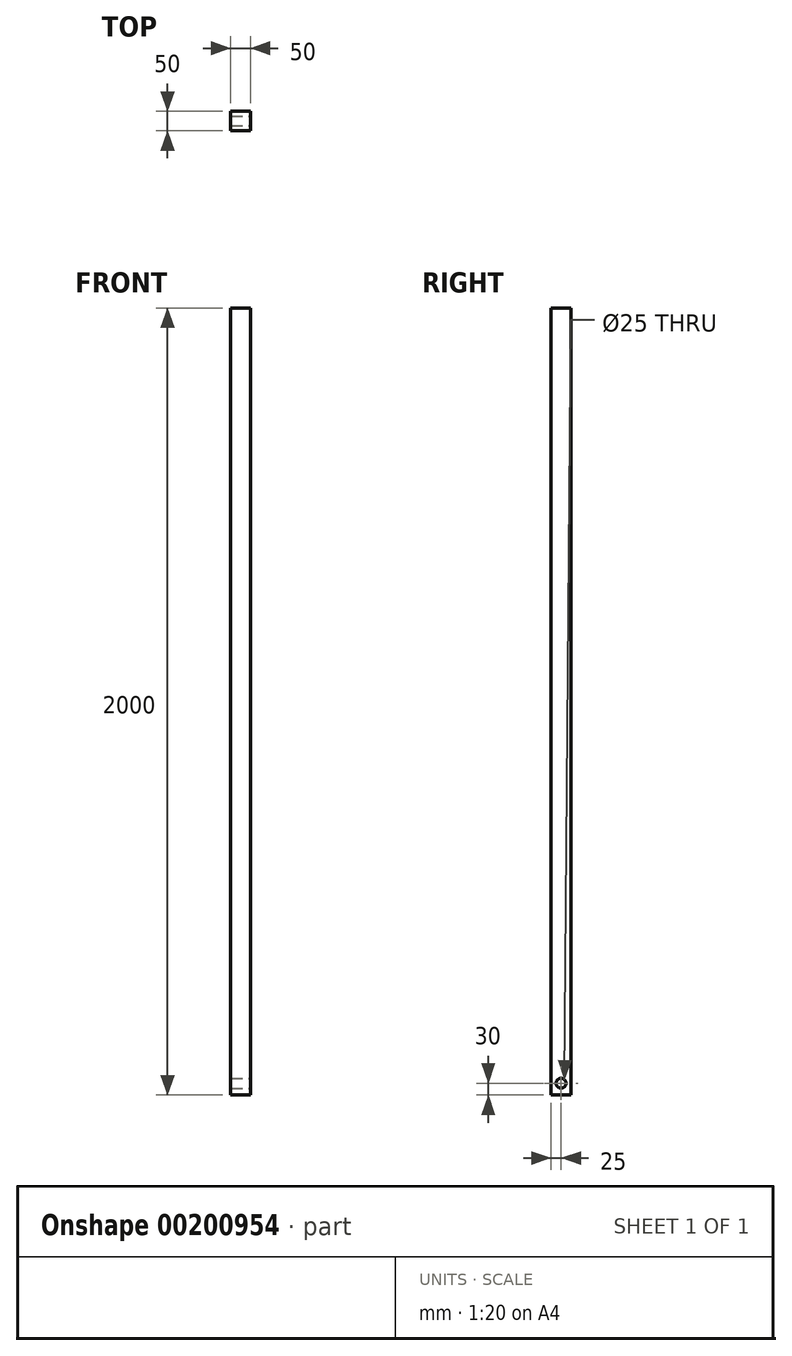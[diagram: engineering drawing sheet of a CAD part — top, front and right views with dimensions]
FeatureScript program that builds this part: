
annotation { "Feature Type Name" : "Feature", "Feature Type Description" : "" }
export const myFeature = defineFeature(function(context is Context, id is Id, definition is map)
    precondition{}
    {
        {
            var Q0;
            Q0=qCreatedBy(makeId("Top.planeOp"),FACE);
            var sketch = newSketch(context, id + "F0", { "sketchPlane" : qUnion([Q0])});
            skLineSegment(sketch, "E0.bottom", {"start": v(25, -25) * mm, "end": v(-25, -25) * mm});
            skLineSegment(sketch, "E0.top", {"start": v(25, 25) * mm, "end": v(-25, 25) * mm});
            skLineSegment(sketch, "E0.left", {"start": v(25, -25) * mm, "end": v(25, 25) * mm});
            skLineSegment(sketch, "E0.right", {"start": v(-25, -25) * mm, "end": v(-25, 25) * mm});
            skPoint(sketch, "E0.middle", {"position": v(0, 0) * mm});
            skSolve(sketch);
        }
        {
            var Q0;
            Q0=makeQuery(id+"F0.imprint","IMPRINT",FACE,{"disambiguationData":[TD([[makeQuery(id+"F0.imprint","IMPRINT",EDGE,{"derivedFrom":sQuery(id+"F0.wireOp",EDGE,"E0.bottom")}),-1.0]])]});
            extrude(context, id + "F1", {"entities" : qUnion([Q0]), "oppositeDirection" : true, "depth" : 2000 * mm});
        }
        {
            var Q0;
            Q0=makeQuery(id+"F1.opExtrude","SWEPT_FACE",FACE,{"disambiguationData":[OSD([sQuery(id+"F0.wireOp",EDGE,"E0.left")])]});
            var sketch = newSketch(context, id + "F2", { "sketchPlane" : qUnion([Q0])});
            skCircle(sketch, "E1", {"center": v(0, -1970) * mm, "radius": 12.5 * mm});
            skSolve(sketch);
        }
        {
            var Q0;
            Q0=makeQuery(id+"F2.imprint","IMPRINT",FACE,{"disambiguationData":[TD([[makeQuery(id+"F2.imprint","IMPRINT",EDGE,{"derivedFrom":sQuery(id+"F2.wireOp",EDGE,"E1")}),1.0]])]});
            extrude(context, id + "F3", {"entities" : qUnion([Q0]), "operationType" : NewBodyOperationType.REMOVE, "endBound" : BoundingType.UP_TO_NEXT, "oppositeDirection" : true, "depth" : 25 * mm});
        }
    });
